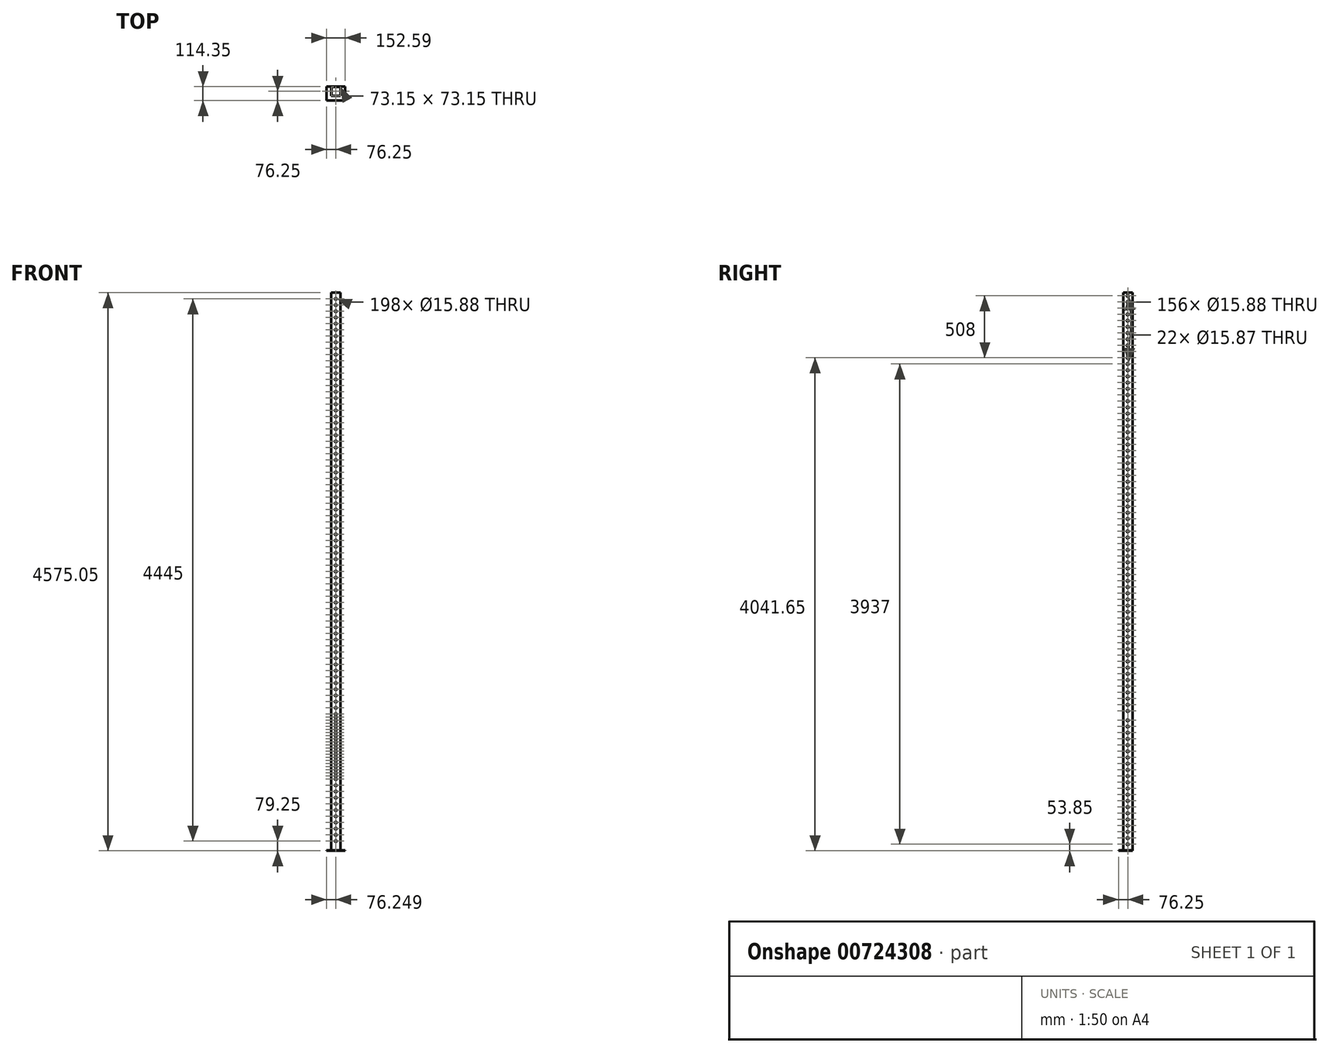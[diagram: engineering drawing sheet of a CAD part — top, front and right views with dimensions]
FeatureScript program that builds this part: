
annotation { "Feature Type Name" : "Feature", "Feature Type Description" : "" }
export const myFeature = defineFeature(function(context is Context, id is Id, definition is map)
    precondition{}
    {
        {
            var Q0;
            Q0=qCreatedBy(makeId("Top.planeOp"),FACE);
            var sketch = newSketch(context, id + "F0", { "sketchPlane" : qUnion([Q0])});
            skLineSegment(sketch, "E0.bottom", {"start": v(-38.1, -38.1) * mm, "end": v(38.1, -38.1) * mm});
            skLineSegment(sketch, "E0.top", {"start": v(-38.1, 38.1) * mm, "end": v(38.1, 38.1) * mm});
            skLineSegment(sketch, "E0.left", {"start": v(-38.1, -38.1) * mm, "end": v(-38.1, 38.1) * mm});
            skLineSegment(sketch, "E0.right", {"start": v(38.1, -38.1) * mm, "end": v(38.1, 38.1) * mm});
            skPoint(sketch, "E0.middle", {"position": v(0, 0) * mm});
            skLineSegment(sketch, "E1.bottom", {"start": v(-36.58, -36.58) * mm, "end": v(36.58, -36.58) * mm});
            skLineSegment(sketch, "E1.top", {"start": v(-36.58, 36.58) * mm, "end": v(36.58, 36.58) * mm});
            skLineSegment(sketch, "E1.left", {"start": v(-36.58, -36.58) * mm, "end": v(-36.58, 36.58) * mm});
            skLineSegment(sketch, "E1.right", {"start": v(36.58, -36.58) * mm, "end": v(36.58, 36.58) * mm});
            skLineSegment(sketch, "E2.bottom", {"start": v(-76.25, -76.25) * mm, "end": v(76.34, -76.25) * mm});
            skLineSegment(sketch, "E2.top", {"start": v(-76.25, 38.1) * mm, "end": v(76.34, 38.1) * mm});
            skLineSegment(sketch, "E2.left", {"start": v(-76.25, -76.25) * mm, "end": v(-76.25, 38.1) * mm});
            skLineSegment(sketch, "E2.right", {"start": v(76.34, -76.25) * mm, "end": v(76.34, 38.1) * mm});
            skSolve(sketch);
        }
        {
            var Q0;
            Q0=makeQuery(id+"F0.imprint","IMPRINT",FACE,{"disambiguationData":[TD([[makeQuery(id+"F0.imprint","IMPRINT",EDGE,{"derivedFrom":sQuery(id+"F0.wireOp",EDGE,"E0.bottom")}),-1.0]])]});
            extrude(context, id + "F1", {"entities" : qUnion([Q0]), "oppositeDirection" : true, "depth" : 3.05 * mm, "offsetDistance" : 25.4 * mm});
        }
        {
            var Q0;
            Q0=makeQuery(id+"F0.imprint","IMPRINT",FACE,{"disambiguationData":[TD([[makeQuery(id+"F0.imprint","IMPRINT",EDGE,{"derivedFrom":sQuery(id+"F0.wireOp",EDGE,"E0.bottom")}),1.0]])]});
            extrude(context, id + "F2", {"entities" : qUnion([Q0]), "operationType" : NewBodyOperationType.ADD, "depth" : 4572 * mm, "offsetDistance" : 25.4 * mm});
        }
        {
            var Q0;
            Q0=qCreatedBy(makeId("Front.planeOp"),FACE);
            cPlane(context, id + "F3", {"entities" : qUnion([Q0]), "cplaneType" : CPlaneType.OFFSET, "offset" : 76.2 * mm, "width" : 152.4 * mm, "height" : 152.4 * mm});
        }
        {
            var Q0;
            Q0=qCreatedBy(makeId("Right.planeOp"),FACE);
            cPlane(context, id + "F4", {"entities" : qUnion([Q0]), "cplaneType" : CPlaneType.OFFSET, "offset" : 76.2 * mm, "width" : 152.4 * mm, "height" : 152.4 * mm});
        }
        {
            var Q0;
            Q0=qCreatedBy(id+"F4.planeOp",FACE);
            var sketch = newSketch(context, id + "F5", { "sketchPlane" : qUnion([Q0])});
            skLineSegment(sketch, "E3.bottom", {"start": v(-38.1, 3657.6) * mm, "end": v(38.1, 3657.6) * mm});
            skLineSegment(sketch, "E3.top", {"start": v(-38.1, 0) * mm, "end": v(38.1, 0) * mm});
            skLineSegment(sketch, "E3.left", {"start": v(-38.1, 3657.6) * mm, "end": v(-38.1, 0) * mm});
            skLineSegment(sketch, "E3.right", {"start": v(38.1, 3657.6) * mm, "end": v(38.1, 0) * mm});
            skPoint(sketch, "E4", {"position": v(0, 50.8) * mm});
            skPoint(sketch, "E5.1.0.0", {"position": v(0, 101.6) * mm});
            skPoint(sketch, "E5.2.0.0", {"position": v(0, 152.4) * mm});
            skPoint(sketch, "E5.3.0.0", {"position": v(0, 203.2) * mm});
            skPoint(sketch, "E5.4.0.0", {"position": v(0, 254) * mm});
            skPoint(sketch, "E5.5.0.0", {"position": v(0, 304.8) * mm});
            skPoint(sketch, "E5.6.0.0", {"position": v(0, 355.6) * mm});
            skPoint(sketch, "E5.7.0.0", {"position": v(0, 406.4) * mm});
            skPoint(sketch, "E5.8.0.0", {"position": v(0, 457.2) * mm});
            skPoint(sketch, "E5.9.0.0", {"position": v(0, 508) * mm});
            skPoint(sketch, "E5.10.0.0", {"position": v(0, 558.8) * mm});
            skPoint(sketch, "E5.11.0.0", {"position": v(0, 609.6) * mm});
            skPoint(sketch, "E5.12.0.0", {"position": v(0, 660.4) * mm});
            skPoint(sketch, "E5.13.0.0", {"position": v(0, 711.2) * mm});
            skPoint(sketch, "E5.14.0.0", {"position": v(0, 762) * mm});
            skPoint(sketch, "E5.15.0.0", {"position": v(0, 812.8) * mm});
            skPoint(sketch, "E5.16.0.0", {"position": v(0, 863.6) * mm});
            skPoint(sketch, "E5.17.0.0", {"position": v(0, 914.4) * mm});
            skPoint(sketch, "E5.18.0.0", {"position": v(0, 965.2) * mm});
            skPoint(sketch, "E5.19.0.0", {"position": v(0, 1016) * mm});
            skPoint(sketch, "E5.20.0.0", {"position": v(0, 1066.8) * mm});
            skLineSegment(sketch, "E5.direction1", {"start": v(0, 50.8) * mm, "end": v(0, 101.6) * mm, "construction": true});
            skPoint(sketch, "E6", {"position": v(0, 1143) * mm});
            skPoint(sketch, "E7.1.0.0", {"position": v(0, 1193.8) * mm});
            skPoint(sketch, "E7.2.0.0", {"position": v(0, 1244.6) * mm});
            skPoint(sketch, "E7.3.0.0", {"position": v(0, 1295.4) * mm});
            skPoint(sketch, "E7.4.0.0", {"position": v(0, 1346.2) * mm});
            skPoint(sketch, "E7.5.0.0", {"position": v(0, 1397) * mm});
            skPoint(sketch, "E7.6.0.0", {"position": v(0, 1447.8) * mm});
            skPoint(sketch, "E7.7.0.0", {"position": v(0, 1498.6) * mm});
            skPoint(sketch, "E7.8.0.0", {"position": v(0, 1549.4) * mm});
            skPoint(sketch, "E7.9.0.0", {"position": v(0, 1600.2) * mm});
            skPoint(sketch, "E7.10.0.0", {"position": v(0, 1651) * mm});
            skPoint(sketch, "E7.11.0.0", {"position": v(0, 1701.8) * mm});
            skPoint(sketch, "E7.12.0.0", {"position": v(0, 1752.6) * mm});
            skPoint(sketch, "E7.13.0.0", {"position": v(0, 1803.4) * mm});
            skPoint(sketch, "E7.14.0.0", {"position": v(0, 1854.2) * mm});
            skPoint(sketch, "E7.15.0.0", {"position": v(0, 1905) * mm});
            skPoint(sketch, "E7.16.0.0", {"position": v(0, 1955.8) * mm});
            skPoint(sketch, "E7.17.0.0", {"position": v(0, 2006.6) * mm});
            skPoint(sketch, "E7.18.0.0", {"position": v(0, 2057.4) * mm});
            skPoint(sketch, "E7.19.0.0", {"position": v(0, 2108.2) * mm});
            skPoint(sketch, "E7.20.0.0", {"position": v(0, 2159) * mm});
            skPoint(sketch, "E7.21.0.0", {"position": v(0, 2209.8) * mm});
            skPoint(sketch, "E7.22.0.0", {"position": v(0, 2260.6) * mm});
            skPoint(sketch, "E7.23.0.0", {"position": v(0, 2311.4) * mm});
            skPoint(sketch, "E7.24.0.0", {"position": v(0, 2362.2) * mm});
            skPoint(sketch, "E7.25.0.0", {"position": v(0, 2413) * mm});
            skPoint(sketch, "E7.26.0.0", {"position": v(0, 2463.8) * mm});
            skPoint(sketch, "E7.27.0.0", {"position": v(0, 2514.6) * mm});
            skPoint(sketch, "E7.28.0.0", {"position": v(0, 2565.4) * mm});
            skPoint(sketch, "E7.29.0.0", {"position": v(0, 2616.2) * mm});
            skLineSegment(sketch, "E7.direction1", {"start": v(0, 1143) * mm, "end": v(0, 1193.8) * mm, "construction": true});
            skPoint(sketch, "E8.0.30.0", {"position": v(0, 2667) * mm});
            skPoint(sketch, "E8.0.31.0", {"position": v(0, 2717.8) * mm});
            skPoint(sketch, "E9.0.32.0", {"position": v(0, 2768.6) * mm});
            skPoint(sketch, "E9.0.33.0", {"position": v(0, 2819.4) * mm});
            skPoint(sketch, "E9.0.34.0", {"position": v(0, 2870.2) * mm});
            skPoint(sketch, "E9.0.35.0", {"position": v(0, 2921) * mm});
            skPoint(sketch, "E9.0.36.0", {"position": v(0, 2971.8) * mm});
            skPoint(sketch, "E9.0.37.0", {"position": v(0, 3022.6) * mm});
            skPoint(sketch, "E9.0.38.0", {"position": v(0, 3073.4) * mm});
            skPoint(sketch, "E9.0.39.0", {"position": v(0, 3124.2) * mm});
            skPoint(sketch, "E9.0.40.0", {"position": v(0, 3175) * mm});
            skPoint(sketch, "E9.0.41.0", {"position": v(0, 3225.8) * mm});
            skPoint(sketch, "E9.0.42.0", {"position": v(0, 3276.6) * mm});
            skPoint(sketch, "E9.0.43.0", {"position": v(0, 3327.4) * mm});
            skPoint(sketch, "E9.0.44.0", {"position": v(0, 3378.2) * mm});
            skPoint(sketch, "E9.0.45.0", {"position": v(0, 3429) * mm});
            skPoint(sketch, "E9.0.46.0", {"position": v(0, 3479.8) * mm});
            skPoint(sketch, "E9.0.47.0", {"position": v(0, 3530.6) * mm});
            skPoint(sketch, "E9.0.48.0", {"position": v(0, 3581.4) * mm});
            skPoint(sketch, "E9.0.49.0", {"position": v(0, 3632.2) * mm});
            skPoint(sketch, "E10.0.50.0", {"position": v(0, 3683) * mm});
            skPoint(sketch, "E10.0.51.0", {"position": v(0, 3733.8) * mm});
            skPoint(sketch, "E10.0.52.0", {"position": v(0, 3784.6) * mm});
            skPoint(sketch, "E10.0.53.0", {"position": v(0, 3835.4) * mm});
            skPoint(sketch, "E10.0.54.0", {"position": v(0, 3886.2) * mm});
            skPoint(sketch, "E10.0.55.0", {"position": v(0, 3937) * mm});
            skPoint(sketch, "E10.0.56.0", {"position": v(0, 3987.8) * mm});
            skPoint(sketch, "E10.0.57.0", {"position": v(0, 4038.6) * mm});
            skPoint(sketch, "E10.0.58.0", {"position": v(0, 4089.4) * mm});
            skPoint(sketch, "E10.0.59.0", {"position": v(0, 4140.2) * mm});
            skPoint(sketch, "E11.0.60.0", {"position": v(0, 4191) * mm});
            skPoint(sketch, "E11.0.61.0", {"position": v(0, 4241.8) * mm});
            skPoint(sketch, "E11.0.62.0", {"position": v(0, 4292.6) * mm});
            skPoint(sketch, "E11.0.63.0", {"position": v(0, 4343.4) * mm});
            skPoint(sketch, "E11.0.64.0", {"position": v(0, 4394.2) * mm});
            skPoint(sketch, "E12.0.65.0", {"position": v(0, 4445) * mm});
            skPoint(sketch, "E12.0.66.0", {"position": v(0, 4495.8) * mm});
            skPoint(sketch, "E13.0.67.0", {"position": v(0, 4546.6) * mm});
            skSolve(sketch);
        }
        {
            var Q0;
            Q0=qCreatedBy(id+"F3.planeOp",FACE);
            var sketch = newSketch(context, id + "F6", { "sketchPlane" : qUnion([Q0])});
            skLineSegment(sketch, "E14.bottom", {"start": v(-38.1, 4572) * mm, "end": v(38.1, 4572) * mm});
            skLineSegment(sketch, "E14.top", {"start": v(-38.1, 0) * mm, "end": v(38.1, 0) * mm});
            skLineSegment(sketch, "E14.left", {"start": v(-38.1, 4572) * mm, "end": v(-38.1, 0) * mm});
            skLineSegment(sketch, "E14.right", {"start": v(38.1, 4572) * mm, "end": v(38.1, 0) * mm});
            skPoint(sketch, "E15", {"position": v(0, 76.2) * mm});
            skPoint(sketch, "E16.1.0.0", {"position": v(0, 127) * mm});
            skPoint(sketch, "E16.2.0.0", {"position": v(0, 177.8) * mm});
            skPoint(sketch, "E16.3.0.0", {"position": v(0, 228.6) * mm});
            skPoint(sketch, "E16.4.0.0", {"position": v(0, 279.4) * mm});
            skPoint(sketch, "E16.5.0.0", {"position": v(0, 330.2) * mm});
            skPoint(sketch, "E16.6.0.0", {"position": v(0, 381) * mm});
            skPoint(sketch, "E16.7.0.0", {"position": v(0, 431.8) * mm});
            skPoint(sketch, "E16.8.0.0", {"position": v(0, 482.6) * mm});
            skPoint(sketch, "E16.9.0.0", {"position": v(0, 533.4) * mm});
            skLineSegment(sketch, "E16.direction1", {"start": v(0, 76.2) * mm, "end": v(0, 127) * mm, "construction": true});
            skPoint(sketch, "E17", {"position": v(0, 1168.4) * mm});
            skPoint(sketch, "E18.1.0.0", {"position": v(0, 1219.2) * mm});
            skPoint(sketch, "E18.2.0.0", {"position": v(0, 1270) * mm});
            skPoint(sketch, "E18.3.0.0", {"position": v(0, 1320.8) * mm});
            skPoint(sketch, "E18.4.0.0", {"position": v(0, 1371.6) * mm});
            skPoint(sketch, "E18.5.0.0", {"position": v(0, 1422.4) * mm});
            skPoint(sketch, "E18.6.0.0", {"position": v(0, 1473.2) * mm});
            skPoint(sketch, "E18.7.0.0", {"position": v(0, 1524) * mm});
            skPoint(sketch, "E18.8.0.0", {"position": v(0, 1574.8) * mm});
            skPoint(sketch, "E18.9.0.0", {"position": v(0, 1625.6) * mm});
            skPoint(sketch, "E18.10.0.0", {"position": v(0, 1676.4) * mm});
            skPoint(sketch, "E18.11.0.0", {"position": v(0, 1727.2) * mm});
            skPoint(sketch, "E18.12.0.0", {"position": v(0, 1778) * mm});
            skPoint(sketch, "E18.13.0.0", {"position": v(0, 1828.8) * mm});
            skPoint(sketch, "E18.14.0.0", {"position": v(0, 1879.6) * mm});
            skPoint(sketch, "E18.15.0.0", {"position": v(0, 1930.4) * mm});
            skPoint(sketch, "E18.16.0.0", {"position": v(0, 1981.2) * mm});
            skPoint(sketch, "E18.17.0.0", {"position": v(0, 2032) * mm});
            skPoint(sketch, "E18.18.0.0", {"position": v(0, 2082.8) * mm});
            skPoint(sketch, "E18.19.0.0", {"position": v(0, 2133.6) * mm});
            skPoint(sketch, "E18.20.0.0", {"position": v(0, 2184.4) * mm});
            skPoint(sketch, "E18.21.0.0", {"position": v(0, 2235.2) * mm});
            skPoint(sketch, "E18.22.0.0", {"position": v(0, 2286) * mm});
            skPoint(sketch, "E18.23.0.0", {"position": v(0, 2336.8) * mm});
            skPoint(sketch, "E18.24.0.0", {"position": v(0, 2387.6) * mm});
            skPoint(sketch, "E18.25.0.0", {"position": v(0, 2438.4) * mm});
            skPoint(sketch, "E18.26.0.0", {"position": v(0, 2489.2) * mm});
            skPoint(sketch, "E18.27.0.0", {"position": v(0, 2540) * mm});
            skPoint(sketch, "E18.28.0.0", {"position": v(0, 2590.8) * mm});
            skPoint(sketch, "E18.29.0.0", {"position": v(0, 2641.6) * mm});
            skLineSegment(sketch, "E18.direction1", {"start": v(0, 1168.4) * mm, "end": v(0, 1219.2) * mm, "construction": true});
            skPoint(sketch, "E19.0.30.0", {"position": v(0, 2692.4) * mm});
            skPoint(sketch, "E20.0.10.0", {"position": v(0, 584.2) * mm});
            skPoint(sketch, "E21.1.0.0", {"position": v(0, 609.6) * mm});
            skPoint(sketch, "E21.2.0.0", {"position": v(0, 635) * mm});
            skPoint(sketch, "E21.3.0.0", {"position": v(0, 660.4) * mm});
            skPoint(sketch, "E21.4.0.0", {"position": v(0, 685.8) * mm});
            skPoint(sketch, "E21.5.0.0", {"position": v(0, 711.2) * mm});
            skPoint(sketch, "E21.6.0.0", {"position": v(0, 736.6) * mm});
            skPoint(sketch, "E21.7.0.0", {"position": v(0, 762) * mm});
            skPoint(sketch, "E21.8.0.0", {"position": v(0, 787.4) * mm});
            skPoint(sketch, "E21.9.0.0", {"position": v(0, 812.8) * mm});
            skPoint(sketch, "E21.10.0.0", {"position": v(0, 838.2) * mm});
            skPoint(sketch, "E21.11.0.0", {"position": v(0, 863.6) * mm});
            skPoint(sketch, "E21.12.0.0", {"position": v(0, 889) * mm});
            skPoint(sketch, "E21.13.0.0", {"position": v(0, 914.4) * mm});
            skPoint(sketch, "E21.14.0.0", {"position": v(0, 939.8) * mm});
            skPoint(sketch, "E21.15.0.0", {"position": v(0, 965.2) * mm});
            skPoint(sketch, "E21.16.0.0", {"position": v(0, 990.6) * mm});
            skPoint(sketch, "E21.17.0.0", {"position": v(0, 1016) * mm});
            skPoint(sketch, "E21.18.0.0", {"position": v(0, 1041.4) * mm});
            skPoint(sketch, "E21.19.0.0", {"position": v(0, 1066.8) * mm});
            skPoint(sketch, "E21.20.0.0", {"position": v(0, 1092.2) * mm});
            skLineSegment(sketch, "E21.direction1", {"start": v(0, 584.2) * mm, "end": v(0, 609.6) * mm, "construction": true});
            skPoint(sketch, "E22.0.21.0", {"position": v(0, 1117.6) * mm});
            skPoint(sketch, "E23.0.32.0", {"position": v(0, 2794) * mm});
            skPoint(sketch, "E23.0.33.0", {"position": v(0, 2844.8) * mm});
            skPoint(sketch, "E23.0.34.0", {"position": v(0, 2895.6) * mm});
            skPoint(sketch, "E23.0.35.0", {"position": v(0, 2946.4) * mm});
            skPoint(sketch, "E23.0.36.0", {"position": v(0, 2997.2) * mm});
            skPoint(sketch, "E23.0.37.0", {"position": v(0, 3048) * mm});
            skPoint(sketch, "E23.0.38.0", {"position": v(0, 3098.8) * mm});
            skPoint(sketch, "E23.0.39.0", {"position": v(0, 3149.6) * mm});
            skPoint(sketch, "E23.0.40.0", {"position": v(0, 3200.4) * mm});
            skPoint(sketch, "E23.0.41.0", {"position": v(0, 3251.2) * mm});
            skPoint(sketch, "E23.0.42.0", {"position": v(0, 3302) * mm});
            skPoint(sketch, "E23.0.43.0", {"position": v(0, 3352.8) * mm});
            skPoint(sketch, "E23.0.44.0", {"position": v(0, 3403.6) * mm});
            skPoint(sketch, "E23.0.45.0", {"position": v(0, 3454.4) * mm});
            skPoint(sketch, "E23.0.46.0", {"position": v(0, 3505.2) * mm});
            skPoint(sketch, "E23.0.47.0", {"position": v(0, 3556) * mm});
            skPoint(sketch, "E23.0.48.0", {"position": v(0, 3606.8) * mm});
            skPoint(sketch, "E24.0.30.0", {"position": v(0, 2743.2) * mm});
            skPoint(sketch, "E25.0.49.0", {"position": v(0, 3657.6) * mm});
            skPoint(sketch, "E25.0.50.0", {"position": v(0, 3708.4) * mm});
            skPoint(sketch, "E25.0.51.0", {"position": v(0, 3759.2) * mm});
            skPoint(sketch, "E25.0.52.0", {"position": v(0, 3810) * mm});
            skPoint(sketch, "E25.0.53.0", {"position": v(0, 3860.8) * mm});
            skPoint(sketch, "E25.0.54.0", {"position": v(0, 3911.6) * mm});
            skPoint(sketch, "E25.0.55.0", {"position": v(0, 3962.4) * mm});
            skPoint(sketch, "E25.0.56.0", {"position": v(0, 4013.2) * mm});
            skPoint(sketch, "E25.0.57.0", {"position": v(0, 4064) * mm});
            skPoint(sketch, "E25.0.58.0", {"position": v(0, 4114.8) * mm});
            skPoint(sketch, "E25.0.59.0", {"position": v(0, 4165.6) * mm});
            skPoint(sketch, "E25.0.60.0", {"position": v(0, 4216.4) * mm});
            skPoint(sketch, "E25.0.61.0", {"position": v(0, 4267.2) * mm});
            skPoint(sketch, "E25.0.62.0", {"position": v(0, 4318) * mm});
            skPoint(sketch, "E25.0.63.0", {"position": v(0, 4368.8) * mm});
            skPoint(sketch, "E25.0.64.0", {"position": v(0, 4419.6) * mm});
            skPoint(sketch, "E25.0.65.0", {"position": v(0, 4470.4) * mm});
            skPoint(sketch, "E25.0.66.0", {"position": v(0, 4521.2) * mm});
            skSolve(sketch);
        }
        {
            var Q0;
            Q0=sQuery(id+"F6.wireOp",VERTEX,"E15");
            var Q1;
            Q1=sQuery(id+"F6.wireOp",VERTEX,"E16.1.0.0");
            var Q2;
            Q2=sQuery(id+"F6.wireOp",VERTEX,"E16.2.0.0");
            var Q3;
            Q3=sQuery(id+"F6.wireOp",VERTEX,"E16.3.0.0");
            var Q4;
            Q4=sQuery(id+"F6.wireOp",VERTEX,"E16.4.0.0");
            var Q5;
            Q5=sQuery(id+"F6.wireOp",VERTEX,"E16.5.0.0");
            var Q6;
            Q6=sQuery(id+"F6.wireOp",VERTEX,"E16.6.0.0");
            var Q7;
            Q7=sQuery(id+"F6.wireOp",VERTEX,"E16.7.0.0");
            var Q8;
            Q8=sQuery(id+"F6.wireOp",VERTEX,"E16.8.0.0");
            var Q9;
            Q9=sQuery(id+"F6.wireOp",VERTEX,"E16.9.0.0");
            var Q10;
            Q10=sQuery(id+"F6.wireOp",VERTEX,"E20.0.10.0");
            var Q11;
            Q11=sQuery(id+"F6.wireOp",VERTEX,"E21.1.0.0");
            var Q12;
            Q12=sQuery(id+"F6.wireOp",VERTEX,"E21.2.0.0");
            var Q13;
            Q13=sQuery(id+"F6.wireOp",VERTEX,"E21.3.0.0");
            var Q14;
            Q14=sQuery(id+"F6.wireOp",VERTEX,"E21.4.0.0");
            var Q15;
            Q15=sQuery(id+"F6.wireOp",VERTEX,"E21.5.0.0");
            var Q16;
            Q16=sQuery(id+"F6.wireOp",VERTEX,"E21.6.0.0");
            var Q17;
            Q17=sQuery(id+"F6.wireOp",VERTEX,"E21.7.0.0");
            var Q18;
            Q18=sQuery(id+"F6.wireOp",VERTEX,"E21.8.0.0");
            var Q19;
            Q19=sQuery(id+"F6.wireOp",VERTEX,"E21.9.0.0");
            var Q20;
            Q20=sQuery(id+"F6.wireOp",VERTEX,"E21.10.0.0");
            var Q21;
            Q21=sQuery(id+"F6.wireOp",VERTEX,"E21.11.0.0");
            var Q22;
            Q22=sQuery(id+"F6.wireOp",VERTEX,"E21.12.0.0");
            var Q23;
            Q23=sQuery(id+"F6.wireOp",VERTEX,"E21.13.0.0");
            var Q24;
            Q24=sQuery(id+"F6.wireOp",VERTEX,"E21.14.0.0");
            var Q25;
            Q25=sQuery(id+"F6.wireOp",VERTEX,"E21.15.0.0");
            var Q26;
            Q26=sQuery(id+"F6.wireOp",VERTEX,"E21.16.0.0");
            var Q27;
            Q27=sQuery(id+"F6.wireOp",VERTEX,"E21.17.0.0");
            var Q28;
            Q28=sQuery(id+"F6.wireOp",VERTEX,"E21.18.0.0");
            var Q29;
            Q29=sQuery(id+"F6.wireOp",VERTEX,"E21.19.0.0");
            var Q30;
            Q30=sQuery(id+"F6.wireOp",VERTEX,"E21.20.0.0");
            var Q31;
            Q31=sQuery(id+"F6.wireOp",VERTEX,"E22.0.21.0");
            var Q32;
            Q32=sQuery(id+"F6.wireOp",VERTEX,"E17");
            var Q33;
            Q33=sQuery(id+"F6.wireOp",VERTEX,"E18.1.0.0");
            var Q34;
            Q34=sQuery(id+"F6.wireOp",VERTEX,"E18.2.0.0");
            var Q35;
            Q35=sQuery(id+"F6.wireOp",VERTEX,"E18.3.0.0");
            var Q36;
            Q36=sQuery(id+"F6.wireOp",VERTEX,"E18.4.0.0");
            var Q37;
            Q37=sQuery(id+"F6.wireOp",VERTEX,"E18.5.0.0");
            var Q38;
            Q38=sQuery(id+"F6.wireOp",VERTEX,"E18.6.0.0");
            var Q39;
            Q39=sQuery(id+"F6.wireOp",VERTEX,"E18.7.0.0");
            var Q40;
            Q40=sQuery(id+"F6.wireOp",VERTEX,"E18.8.0.0");
            var Q41;
            Q41=sQuery(id+"F6.wireOp",VERTEX,"E18.9.0.0");
            var Q42;
            Q42=sQuery(id+"F6.wireOp",VERTEX,"E18.10.0.0");
            var Q43;
            Q43=sQuery(id+"F6.wireOp",VERTEX,"E18.11.0.0");
            var Q44;
            Q44=sQuery(id+"F6.wireOp",VERTEX,"E18.12.0.0");
            var Q45;
            Q45=sQuery(id+"F6.wireOp",VERTEX,"E18.13.0.0");
            var Q46;
            Q46=sQuery(id+"F6.wireOp",VERTEX,"E18.14.0.0");
            var Q47;
            Q47=sQuery(id+"F6.wireOp",VERTEX,"E18.15.0.0");
            var Q48;
            Q48=sQuery(id+"F6.wireOp",VERTEX,"E18.16.0.0");
            var Q49;
            Q49=sQuery(id+"F6.wireOp",VERTEX,"E18.17.0.0");
            var Q50;
            Q50=sQuery(id+"F6.wireOp",VERTEX,"E18.18.0.0");
            var Q51;
            Q51=sQuery(id+"F6.wireOp",VERTEX,"E18.19.0.0");
            var Q52;
            Q52=sQuery(id+"F6.wireOp",VERTEX,"E18.20.0.0");
            var Q53;
            Q53=sQuery(id+"F6.wireOp",VERTEX,"E18.21.0.0");
            var Q54;
            Q54=sQuery(id+"F6.wireOp",VERTEX,"E18.22.0.0");
            var Q55;
            Q55=sQuery(id+"F6.wireOp",VERTEX,"E18.23.0.0");
            var Q56;
            Q56=sQuery(id+"F6.wireOp",VERTEX,"E18.24.0.0");
            var Q57;
            Q57=sQuery(id+"F6.wireOp",VERTEX,"E18.25.0.0");
            var Q58;
            Q58=sQuery(id+"F6.wireOp",VERTEX,"E18.26.0.0");
            var Q59;
            Q59=sQuery(id+"F6.wireOp",VERTEX,"E18.27.0.0");
            var Q60;
            Q60=sQuery(id+"F6.wireOp",VERTEX,"E18.28.0.0");
            var Q61;
            Q61=sQuery(id+"F6.wireOp",VERTEX,"E18.29.0.0");
            var Q62;
            Q62=sQuery(id+"F6.wireOp",VERTEX,"E19.0.30.0");
            var Q63;
            Q63=sQuery(id+"F6.wireOp",VERTEX,"E23.0.32.0");
            var Q64;
            Q64=sQuery(id+"F6.wireOp",VERTEX,"E23.0.33.0");
            var Q65;
            Q65=sQuery(id+"F6.wireOp",VERTEX,"E23.0.34.0");
            var Q66;
            Q66=sQuery(id+"F6.wireOp",VERTEX,"E23.0.35.0");
            var Q67;
            Q67=sQuery(id+"F6.wireOp",VERTEX,"E23.0.36.0");
            var Q68;
            Q68=sQuery(id+"F6.wireOp",VERTEX,"E23.0.37.0");
            var Q69;
            Q69=sQuery(id+"F6.wireOp",VERTEX,"E23.0.38.0");
            var Q70;
            Q70=sQuery(id+"F6.wireOp",VERTEX,"E23.0.39.0");
            var Q71;
            Q71=sQuery(id+"F6.wireOp",VERTEX,"E23.0.40.0");
            var Q72;
            Q72=sQuery(id+"F6.wireOp",VERTEX,"E23.0.41.0");
            var Q73;
            Q73=sQuery(id+"F6.wireOp",VERTEX,"E23.0.42.0");
            var Q74;
            Q74=sQuery(id+"F6.wireOp",VERTEX,"E23.0.43.0");
            var Q75;
            Q75=sQuery(id+"F6.wireOp",VERTEX,"E23.0.44.0");
            var Q76;
            Q76=sQuery(id+"F6.wireOp",VERTEX,"E23.0.45.0");
            var Q77;
            Q77=sQuery(id+"F6.wireOp",VERTEX,"E23.0.46.0");
            var Q78;
            Q78=sQuery(id+"F6.wireOp",VERTEX,"E23.0.47.0");
            var Q79;
            Q79=sQuery(id+"F6.wireOp",VERTEX,"E23.0.48.0");
            var Q80;
            Q80=sQuery(id+"F6.wireOp",VERTEX,"E24.0.30.0");
            var Q81;
            Q81=sQuery(id+"F6.wireOp",VERTEX,"E25.0.49.0");
            var Q82;
            Q82=sQuery(id+"F6.wireOp",VERTEX,"E25.0.50.0");
            var Q83;
            Q83=sQuery(id+"F6.wireOp",VERTEX,"E25.0.51.0");
            var Q84;
            Q84=sQuery(id+"F6.wireOp",VERTEX,"E25.0.52.0");
            var Q85;
            Q85=sQuery(id+"F6.wireOp",VERTEX,"E25.0.53.0");
            var Q86;
            Q86=sQuery(id+"F6.wireOp",VERTEX,"E25.0.54.0");
            var Q87;
            Q87=sQuery(id+"F6.wireOp",VERTEX,"E25.0.55.0");
            var Q88;
            Q88=sQuery(id+"F6.wireOp",VERTEX,"E25.0.56.0");
            var Q89;
            Q89=sQuery(id+"F6.wireOp",VERTEX,"E25.0.57.0");
            var Q90;
            Q90=sQuery(id+"F6.wireOp",VERTEX,"E25.0.58.0");
            var Q91;
            Q91=sQuery(id+"F6.wireOp",VERTEX,"E25.0.59.0");
            var Q92;
            Q92=sQuery(id+"F6.wireOp",VERTEX,"E25.0.60.0");
            var Q93;
            Q93=sQuery(id+"F6.wireOp",VERTEX,"E25.0.61.0");
            var Q94;
            Q94=sQuery(id+"F6.wireOp",VERTEX,"E25.0.62.0");
            var Q95;
            Q95=sQuery(id+"F6.wireOp",VERTEX,"E25.0.63.0");
            var Q96;
            Q96=sQuery(id+"F6.wireOp",VERTEX,"E25.0.64.0");
            var Q97;
            Q97=sQuery(id+"F6.wireOp",VERTEX,"E25.0.65.0");
            var Q98;
            Q98=sQuery(id+"F6.wireOp",VERTEX,"E25.0.66.0");
            var Q99;
            {var subQ0=sQuery(id+"F0.wireOp",EDGE,"E0.right");var subQ1=sQuery(id+"F0.wireOp",EDGE,"E0.left");var subQ2=sQuery(id+"F0.wireOp",EDGE,"E0.top");var subQ3=sQuery(id+"F0.wireOp",EDGE,"E0.bottom");Q99=makeQuery(id+"F2.boolean.opBoolean","MERGE",BODY,{"derivedFrom":[makeQuery(id+"F1.opExtrude","SWEPT_BODY",BODY,{"disambiguationData":[OSD([subQ3,subQ2,subQ1,subQ0,sQuery(id+"F0.wireOp",EDGE,"E2.bottom"),sQuery(id+"F0.wireOp",EDGE,"E2.top"),sQuery(id+"F0.wireOp",EDGE,"E2.left"),sQuery(id+"F0.wireOp",EDGE,"E2.right")])]}),makeQuery(id+"F2.opExtrude","SWEPT_BODY",BODY,{"disambiguationData":[OSD([subQ3,subQ2,subQ1,subQ0,sQuery(id+"F0.wireOp",EDGE,"E1.bottom"),sQuery(id+"F0.wireOp",EDGE,"E1.top"),sQuery(id+"F0.wireOp",EDGE,"E1.left"),sQuery(id+"F0.wireOp",EDGE,"E1.right")])]})]});}
            hole(context, id + "F7", {"style" : HoleStyle.SIMPLE, "endStyle" : HoleEndStyle.THROUGH, "holeDiameter" : 15.88 * mm, "majorDiameter" : 6.35 * mm, "isTappedThrough" : true, "tappedDepth" : 12.7 * mm, "tapClearance" : 3, "locations" : qUnion([Q0, Q1, Q2, Q3, Q4, Q5, Q6, Q7, Q8, Q9, Q10, Q11, Q12, Q13, Q14, Q15, Q16, Q17, Q18, Q19, Q20, Q21, Q22, Q23, Q24, Q25, Q26, Q27, Q28, Q29, Q30, Q31, Q32, Q33, Q34, Q35, Q36, Q37, Q38, Q39, Q40, Q41, Q42, Q43, Q44, Q45, Q46, Q47, Q48, Q49, Q50, Q51, Q52, Q53, Q54, Q55, Q56, Q57, Q58, Q59, Q60, Q61, Q62, Q63, Q64, Q65, Q66, Q67, Q68, Q69, Q70, Q71, Q72, Q73, Q74, Q75, Q76, Q77, Q78, Q79, Q80, Q81, Q82, Q83, Q84, Q85, Q86, Q87, Q88, Q89, Q90, Q91, Q92, Q93, Q94, Q95, Q96, Q97, Q98]), "scope" : qUnion([Q99])});
        }
        {
            var Q0;
            Q0=sQuery(id+"F5.wireOp",VERTEX,"E4");
            var Q1;
            Q1=sQuery(id+"F5.wireOp",VERTEX,"E5.1.0.0");
            var Q2;
            Q2=sQuery(id+"F5.wireOp",VERTEX,"E5.2.0.0");
            var Q3;
            Q3=sQuery(id+"F5.wireOp",VERTEX,"E5.3.0.0");
            var Q4;
            Q4=sQuery(id+"F5.wireOp",VERTEX,"E5.4.0.0");
            var Q5;
            Q5=sQuery(id+"F5.wireOp",VERTEX,"E5.5.0.0");
            var Q6;
            Q6=sQuery(id+"F5.wireOp",VERTEX,"E5.6.0.0");
            var Q7;
            Q7=sQuery(id+"F5.wireOp",VERTEX,"E5.7.0.0");
            var Q8;
            Q8=sQuery(id+"F5.wireOp",VERTEX,"E5.8.0.0");
            var Q9;
            Q9=sQuery(id+"F5.wireOp",VERTEX,"E5.9.0.0");
            var Q10;
            Q10=sQuery(id+"F5.wireOp",VERTEX,"E5.10.0.0");
            var Q11;
            Q11=sQuery(id+"F5.wireOp",VERTEX,"E5.11.0.0");
            var Q12;
            Q12=sQuery(id+"F5.wireOp",VERTEX,"E5.12.0.0");
            var Q13;
            Q13=sQuery(id+"F5.wireOp",VERTEX,"E5.13.0.0");
            var Q14;
            Q14=sQuery(id+"F5.wireOp",VERTEX,"E5.14.0.0");
            var Q15;
            Q15=sQuery(id+"F5.wireOp",VERTEX,"E5.15.0.0");
            var Q16;
            Q16=sQuery(id+"F5.wireOp",VERTEX,"E5.16.0.0");
            var Q17;
            Q17=sQuery(id+"F5.wireOp",VERTEX,"E5.17.0.0");
            var Q18;
            Q18=sQuery(id+"F5.wireOp",VERTEX,"E5.18.0.0");
            var Q19;
            Q19=sQuery(id+"F5.wireOp",VERTEX,"E5.19.0.0");
            var Q20;
            Q20=sQuery(id+"F5.wireOp",VERTEX,"E5.20.0.0");
            var Q21;
            Q21=sQuery(id+"F5.wireOp",VERTEX,"E6");
            var Q22;
            Q22=sQuery(id+"F5.wireOp",VERTEX,"E7.1.0.0");
            var Q23;
            Q23=sQuery(id+"F5.wireOp",VERTEX,"E7.2.0.0");
            var Q24;
            Q24=sQuery(id+"F5.wireOp",VERTEX,"E7.3.0.0");
            var Q25;
            Q25=sQuery(id+"F5.wireOp",VERTEX,"E7.4.0.0");
            var Q26;
            Q26=sQuery(id+"F5.wireOp",VERTEX,"E7.5.0.0");
            var Q27;
            Q27=sQuery(id+"F5.wireOp",VERTEX,"E7.6.0.0");
            var Q28;
            Q28=sQuery(id+"F5.wireOp",VERTEX,"E7.7.0.0");
            var Q29;
            Q29=sQuery(id+"F5.wireOp",VERTEX,"E7.8.0.0");
            var Q30;
            Q30=sQuery(id+"F5.wireOp",VERTEX,"E7.9.0.0");
            var Q31;
            Q31=sQuery(id+"F5.wireOp",VERTEX,"E7.10.0.0");
            var Q32;
            Q32=sQuery(id+"F5.wireOp",VERTEX,"E7.11.0.0");
            var Q33;
            Q33=sQuery(id+"F5.wireOp",VERTEX,"E7.12.0.0");
            var Q34;
            Q34=sQuery(id+"F5.wireOp",VERTEX,"E7.13.0.0");
            var Q35;
            Q35=sQuery(id+"F5.wireOp",VERTEX,"E7.14.0.0");
            var Q36;
            Q36=sQuery(id+"F5.wireOp",VERTEX,"E7.15.0.0");
            var Q37;
            Q37=sQuery(id+"F5.wireOp",VERTEX,"E7.16.0.0");
            var Q38;
            Q38=sQuery(id+"F5.wireOp",VERTEX,"E7.17.0.0");
            var Q39;
            Q39=sQuery(id+"F5.wireOp",VERTEX,"E7.18.0.0");
            var Q40;
            Q40=sQuery(id+"F5.wireOp",VERTEX,"E7.19.0.0");
            var Q41;
            Q41=sQuery(id+"F5.wireOp",VERTEX,"E7.20.0.0");
            var Q42;
            Q42=sQuery(id+"F5.wireOp",VERTEX,"E7.21.0.0");
            var Q43;
            Q43=sQuery(id+"F5.wireOp",VERTEX,"E7.22.0.0");
            var Q44;
            Q44=sQuery(id+"F5.wireOp",VERTEX,"E7.23.0.0");
            var Q45;
            Q45=sQuery(id+"F5.wireOp",VERTEX,"E7.24.0.0");
            var Q46;
            Q46=sQuery(id+"F5.wireOp",VERTEX,"E7.25.0.0");
            var Q47;
            Q47=sQuery(id+"F5.wireOp",VERTEX,"E7.26.0.0");
            var Q48;
            Q48=sQuery(id+"F5.wireOp",VERTEX,"E7.27.0.0");
            var Q49;
            Q49=sQuery(id+"F5.wireOp",VERTEX,"E7.28.0.0");
            var Q50;
            Q50=sQuery(id+"F5.wireOp",VERTEX,"E7.29.0.0");
            var Q51;
            Q51=sQuery(id+"F5.wireOp",VERTEX,"E8.0.30.0");
            var Q52;
            Q52=sQuery(id+"F5.wireOp",VERTEX,"E8.0.31.0");
            var Q53;
            Q53=sQuery(id+"F5.wireOp",VERTEX,"E9.0.33.0");
            var Q54;
            Q54=sQuery(id+"F5.wireOp",VERTEX,"E9.0.34.0");
            var Q55;
            Q55=sQuery(id+"F5.wireOp",VERTEX,"E9.0.32.0");
            var Q56;
            Q56=sQuery(id+"F5.wireOp",VERTEX,"E9.0.35.0");
            var Q57;
            Q57=sQuery(id+"F5.wireOp",VERTEX,"E9.0.36.0");
            var Q58;
            Q58=sQuery(id+"F5.wireOp",VERTEX,"E9.0.37.0");
            var Q59;
            Q59=sQuery(id+"F5.wireOp",VERTEX,"E9.0.38.0");
            var Q60;
            Q60=sQuery(id+"F5.wireOp",VERTEX,"E9.0.39.0");
            var Q61;
            Q61=sQuery(id+"F5.wireOp",VERTEX,"E9.0.40.0");
            var Q62;
            Q62=sQuery(id+"F5.wireOp",VERTEX,"E9.0.41.0");
            var Q63;
            Q63=sQuery(id+"F5.wireOp",VERTEX,"E9.0.42.0");
            var Q64;
            Q64=sQuery(id+"F5.wireOp",VERTEX,"E9.0.43.0");
            var Q65;
            Q65=sQuery(id+"F5.wireOp",VERTEX,"E9.0.44.0");
            var Q66;
            Q66=sQuery(id+"F5.wireOp",VERTEX,"E9.0.45.0");
            var Q67;
            Q67=sQuery(id+"F5.wireOp",VERTEX,"E9.0.46.0");
            var Q68;
            Q68=sQuery(id+"F5.wireOp",VERTEX,"E9.0.47.0");
            var Q69;
            Q69=sQuery(id+"F5.wireOp",VERTEX,"E9.0.48.0");
            var Q70;
            Q70=sQuery(id+"F5.wireOp",VERTEX,"E9.0.49.0");
            var Q71;
            Q71=sQuery(id+"F5.wireOp",VERTEX,"E10.0.50.0");
            var Q72;
            Q72=sQuery(id+"F5.wireOp",VERTEX,"E10.0.51.0");
            var Q73;
            Q73=sQuery(id+"F5.wireOp",VERTEX,"E10.0.52.0");
            var Q74;
            Q74=sQuery(id+"F5.wireOp",VERTEX,"E10.0.53.0");
            var Q75;
            Q75=sQuery(id+"F5.wireOp",VERTEX,"E10.0.54.0");
            var Q76;
            Q76=sQuery(id+"F5.wireOp",VERTEX,"E10.0.55.0");
            var Q77;
            Q77=sQuery(id+"F5.wireOp",VERTEX,"E10.0.56.0");
            var Q78;
            Q78=sQuery(id+"F5.wireOp",VERTEX,"E10.0.57.0");
            var Q79;
            Q79=sQuery(id+"F5.wireOp",VERTEX,"E10.0.58.0");
            var Q80;
            Q80=sQuery(id+"F5.wireOp",VERTEX,"E10.0.59.0");
            var Q81;
            Q81=sQuery(id+"F5.wireOp",VERTEX,"E11.0.60.0");
            var Q82;
            Q82=sQuery(id+"F5.wireOp",VERTEX,"E11.0.61.0");
            var Q83;
            Q83=sQuery(id+"F5.wireOp",VERTEX,"E11.0.62.0");
            var Q84;
            Q84=sQuery(id+"F5.wireOp",VERTEX,"E11.0.63.0");
            var Q85;
            Q85=sQuery(id+"F5.wireOp",VERTEX,"E11.0.64.0");
            var Q86;
            Q86=sQuery(id+"F5.wireOp",VERTEX,"E12.0.65.0");
            var Q87;
            Q87=sQuery(id+"F5.wireOp",VERTEX,"E12.0.66.0");
            var Q88;
            Q88=sQuery(id+"F5.wireOp",VERTEX,"E13.0.67.0");
            var Q89;
            {var subQ0=sQuery(id+"F0.wireOp",EDGE,"E0.right");var subQ1=sQuery(id+"F0.wireOp",EDGE,"E0.left");var subQ2=sQuery(id+"F0.wireOp",EDGE,"E0.top");var subQ3=sQuery(id+"F0.wireOp",EDGE,"E0.bottom");Q89=makeQuery(id+"F2.boolean.opBoolean","MERGE",BODY,{"derivedFrom":[makeQuery(id+"F1.opExtrude","SWEPT_BODY",BODY,{"disambiguationData":[OSD([subQ3,subQ2,subQ1,subQ0,sQuery(id+"F0.wireOp",EDGE,"E2.bottom"),sQuery(id+"F0.wireOp",EDGE,"E2.top"),sQuery(id+"F0.wireOp",EDGE,"E2.left"),sQuery(id+"F0.wireOp",EDGE,"E2.right")])]}),makeQuery(id+"F2.opExtrude","SWEPT_BODY",BODY,{"disambiguationData":[OSD([subQ3,subQ2,subQ1,subQ0,sQuery(id+"F0.wireOp",EDGE,"E1.bottom"),sQuery(id+"F0.wireOp",EDGE,"E1.top"),sQuery(id+"F0.wireOp",EDGE,"E1.left"),sQuery(id+"F0.wireOp",EDGE,"E1.right")])]})]});}
            hole(context, id + "F8", {"style" : HoleStyle.SIMPLE, "endStyle" : HoleEndStyle.THROUGH, "holeDiameter" : 15.88 * mm, "majorDiameter" : 6.35 * mm, "isTappedThrough" : true, "tappedDepth" : 12.7 * mm, "tapClearance" : 3, "locations" : qUnion([Q0, Q1, Q2, Q3, Q4, Q5, Q6, Q7, Q8, Q9, Q10, Q11, Q12, Q13, Q14, Q15, Q16, Q17, Q18, Q19, Q20, Q21, Q22, Q23, Q24, Q25, Q26, Q27, Q28, Q29, Q30, Q31, Q32, Q33, Q34, Q35, Q36, Q37, Q38, Q39, Q40, Q41, Q42, Q43, Q44, Q45, Q46, Q47, Q48, Q49, Q50, Q51, Q52, Q53, Q54, Q55, Q56, Q57, Q58, Q59, Q60, Q61, Q62, Q63, Q64, Q65, Q66, Q67, Q68, Q69, Q70, Q71, Q72, Q73, Q74, Q75, Q76, Q77, Q78, Q79, Q80, Q81, Q82, Q83, Q84, Q85, Q86, Q87, Q88]), "scope" : qUnion([Q89])});
        }
    });
